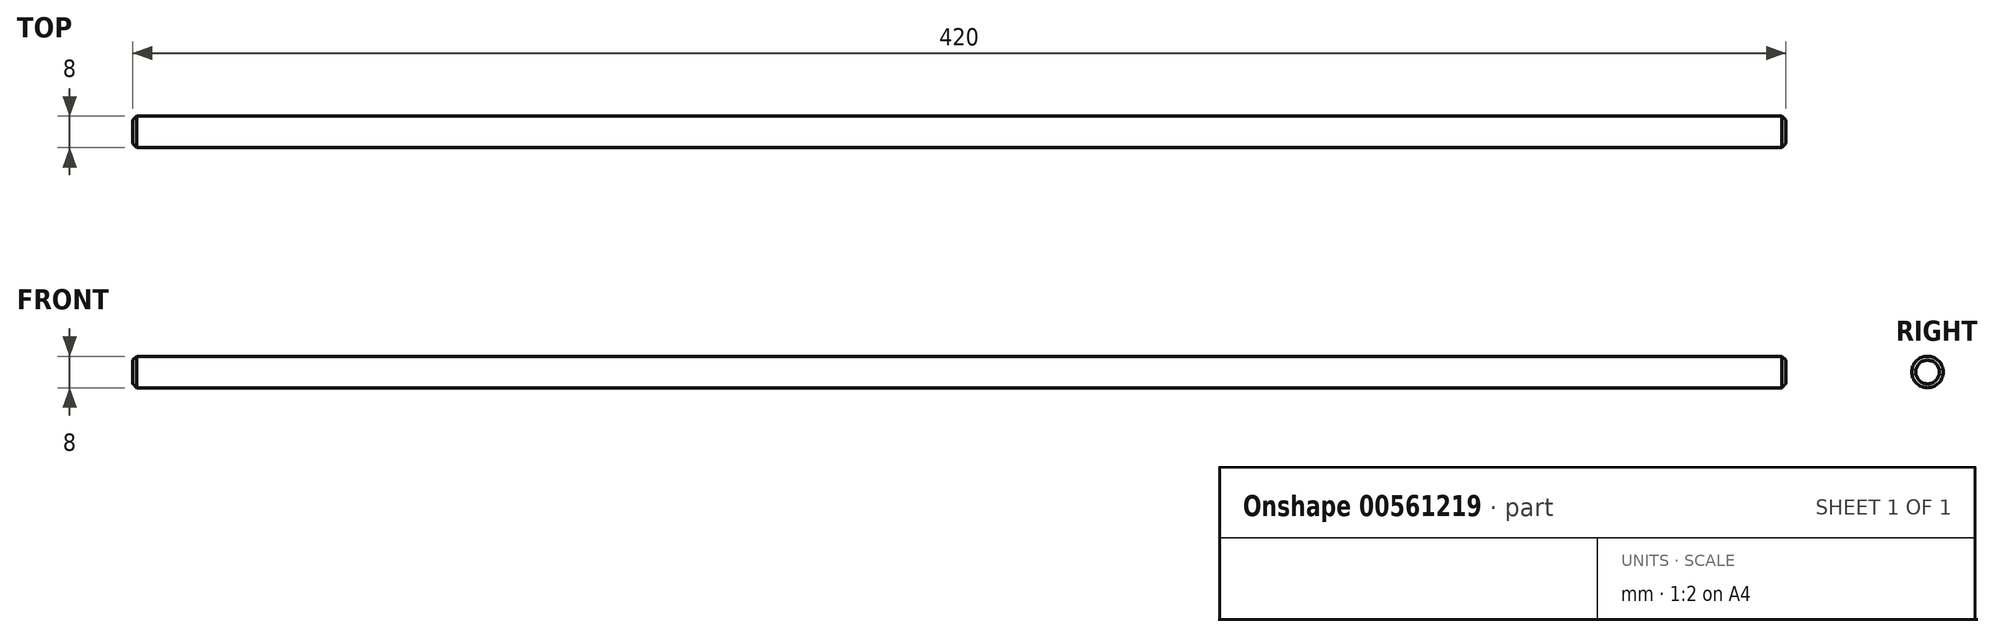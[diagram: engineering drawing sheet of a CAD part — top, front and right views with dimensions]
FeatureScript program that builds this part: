
annotation { "Feature Type Name" : "Feature", "Feature Type Description" : "" }
export const myFeature = defineFeature(function(context is Context, id is Id, definition is map)
    precondition{}
    {
        {
            var Q0;
            Q0=qCreatedBy(makeId("Right.planeOp"),FACE);
            var sketch = newSketch(context, id + "F0", { "sketchPlane" : qUnion([Q0])});
            skCircle(sketch, "E0", {"center": v(0, 0) * mm, "radius": 4 * mm});
            skSolve(sketch);
        }
        {
            var Q0;
            Q0=qSketchRegion(id+"F0",true);
            extrude(context, id + "F1", {"entities" : qUnion([Q0]), "endBound" : BoundingType.SYMMETRIC, "depth" : 420 * mm, "offsetDistance" : 25 * mm});
        }
        {
            var Q0;
            Q0=makeQuery(id+"F1.opExtrude","CAP_EDGE",EDGE,{"disambiguationData":[OSD([sQuery(id+"F0.wireOp",EDGE,"E0")])],"isStart":false});
            var Q1;
            Q1=makeQuery(id+"F1.opExtrude","CAP_EDGE",EDGE,{"disambiguationData":[OSD([sQuery(id+"F0.wireOp",EDGE,"E0")])],"isStart":true});
            chamfer(context, id + "F2", {"entities" : qUnion([Q0, Q1]), "width" : 1 * mm, "tangentPropagation" : true});
        }
    });
